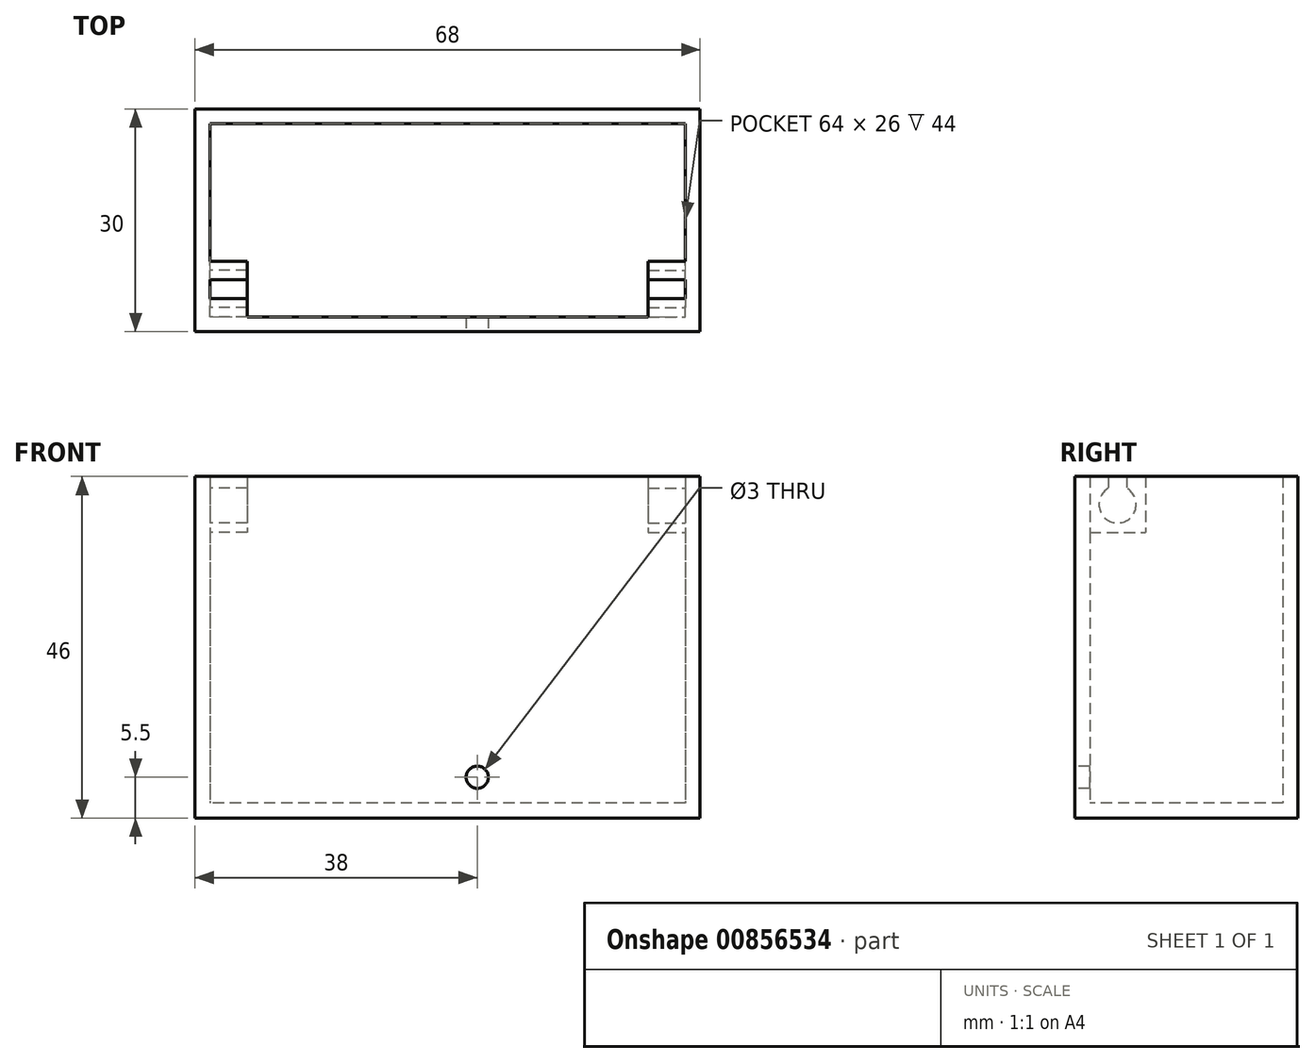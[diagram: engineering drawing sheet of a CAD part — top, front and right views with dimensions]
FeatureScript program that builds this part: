
annotation { "Feature Type Name" : "Feature", "Feature Type Description" : "" }
export const myFeature = defineFeature(function(context is Context, id is Id, definition is map)
    precondition{}
    {
        {
            var Q0;
            Q0=qCreatedBy(makeId("Top.planeOp"),FACE);
            var sketch = newSketch(context, id + "F0", { "sketchPlane" : qUnion([Q0])});
            skLineSegment(sketch, "E0.bottom", {"start": v(32, 13) * mm, "end": v(-32, 13) * mm});
            skLineSegment(sketch, "E0.top", {"start": v(32, -13) * mm, "end": v(-32, -13) * mm});
            skLineSegment(sketch, "E0.left", {"start": v(32, 13) * mm, "end": v(32, -13) * mm});
            skLineSegment(sketch, "E0.right", {"start": v(-32, 13) * mm, "end": v(-32, -13) * mm});
            skPoint(sketch, "E0.middle", {"position": v(0, 0) * mm});
            skLineSegment(sketch, "E1.bottom", {"start": v(34, 15) * mm, "end": v(-34, 15) * mm});
            skLineSegment(sketch, "E1.top", {"start": v(34, -15) * mm, "end": v(-34, -15) * mm});
            skLineSegment(sketch, "E1.left", {"start": v(34, 15) * mm, "end": v(34, -15) * mm});
            skLineSegment(sketch, "E1.right", {"start": v(-34, 15) * mm, "end": v(-34, -15) * mm});
            skSolve(sketch);
        }
        {
            var Q0;
            Q0 = qSketchRegion(id + "F0", true);
            extrude(context, id + "F1", {"entities" : qUnion([Q0]), "depth" : 46 * mm, "offsetDistance" : 25 * mm});
        }
        {
            var Q0;
            Q0 = qSketchRegion(id + "F0", true);
            var Q1;
            Q1=makeQuery(id+"F0.imprint","IMPRINT",FACE,{"disambiguationData":[TD([[makeQuery(id+"F0.imprint","IMPRINT",EDGE,{"derivedFrom":sQuery(id+"F0.wireOp",EDGE,"E0.bottom")}),1.0]])]});
            extrude(context, id + "F2", {"entities" : qUnion([Q0, Q1]), "operationType" : NewBodyOperationType.ADD, "depth" : 2 * mm, "offsetDistance" : 25 * mm});
        }
        {
            var Q0;
            Q0=makeQuery(id+"F1.opExtrude","SWEPT_FACE",FACE,{"disambiguationData":[OSD([sQuery(id+"F0.wireOp",EDGE,"E1.top")])]});
            var sketch = newSketch(context, id + "F3", { "sketchPlane" : qUnion([Q0])});
            skLineSegment(sketch, "E2", {"start": v(-34, 7) * mm, "end": v(34, 7) * mm, "construction": true});
            skCircle(sketch, "E3", {"center": v(4, 5.5) * mm, "radius": 1.5 * mm});
            skSolve(sketch);
        }
        {
            var Q0;
            Q0=makeQuery(id+"F3.imprint","IMPRINT",FACE,{"disambiguationData":[TD([[makeQuery(id+"F3.imprint","IMPRINT",EDGE,{"derivedFrom":sQuery(id+"F3.wireOp",EDGE,"E3")}),1.0]])]});
            var Q1;
            Q1=sQuery(id+"F3.wireOp",EDGE,"E3");
            extrude(context, id + "F4", {"entities" : qUnion([Q0]), "operationType" : NewBodyOperationType.REMOVE, "surfaceEntities" : qUnion([Q1]), "oppositeDirection" : true, "depth" : 3 * mm, "offsetDistance" : 25 * mm});
        }
        {
            var Q0;
            Q0=makeQuery(id+"F1.opExtrude","SWEPT_FACE",FACE,{"disambiguationData":[OSD([sQuery(id+"F0.wireOp",EDGE,"E0.right")])]});
            var sketch = newSketch(context, id + "F5", { "sketchPlane" : qUnion([Q0])});
            skLineSegment(sketch, "E4.bottom", {"start": v(-13, 46) * mm, "end": v(-5.5, 46) * mm});
            skLineSegment(sketch, "E4.top", {"start": v(-13, 38.5) * mm, "end": v(-5.5, 38.5) * mm});
            skLineSegment(sketch, "E4.left", {"start": v(-13, 46) * mm, "end": v(-13, 38.5) * mm});
            skLineSegment(sketch, "E4.right", {"start": v(-5.5, 46) * mm, "end": v(-5.5, 38.5) * mm});
            skLineSegment(sketch, "E5.bottom", {"start": v(-8, 46) * mm, "end": v(-10.5, 46) * mm});
            skLineSegment(sketch, "E5.top", {"start": v(-8, 38.5) * mm, "end": v(-10.5, 38.5) * mm});
            skLineSegment(sketch, "E5.left", {"start": v(-8, 46) * mm, "end": v(-8, 44.42) * mm});
            skLineSegment(sketch, "E5.right", {"start": v(-10.5, 46) * mm, "end": v(-10.5, 44.42) * mm});
            skPoint(sketch, "E5.middle", {"position": v(-9.25, 42.25) * mm});
            skPoint(sketch, "E6.orphan", {"position": v(-9.25, 38.5) * mm});
            skPoint(sketch, "E7.start.orphan", {"position": v(-9.25, 46) * mm});
            skArc(sketch, "E8", {"start": v(-10.5, 44.42) * mm, "mid": v(-9.25, 39.75) * mm, "end": v(-8, 44.42) * mm});
            skSolve(sketch);
        }
        {
            var Q0;
            {var subQ3=sQuery(id+"F5.wireOp",EDGE,"E4.left");Q0=makeQuery(id+"F5.imprint","IMPRINT",FACE,{"disambiguationData":[TD([[makeQuery(id+"F5.imprint","IMPRINT",EDGE,{"derivedFrom":subQ3}),1.0]])]});}
            extrude(context, id + "F6", {"entities" : qUnion([Q0]), "operationType" : NewBodyOperationType.ADD, "depth" : 5 * mm, "offsetDistance" : 25 * mm});
        }
        {
            var Q0;
            Q0=makeQuery(id+"F1.opExtrude","SWEPT_FACE",FACE,{"disambiguationData":[OSD([sQuery(id+"F0.wireOp",EDGE,"E0.left")])]});
            var sketch = newSketch(context, id + "F7", { "sketchPlane" : qUnion([Q0])});
            skLineSegment(sketch, "E9.bottom", {"start": v(13, 46) * mm, "end": v(5.5, 46) * mm});
            skLineSegment(sketch, "E9.top", {"start": v(13, 38.5) * mm, "end": v(5.5, 38.5) * mm});
            skLineSegment(sketch, "E9.left", {"start": v(13, 46) * mm, "end": v(13, 38.5) * mm});
            skLineSegment(sketch, "E9.right", {"start": v(5.5, 46) * mm, "end": v(5.5, 38.5) * mm});
            skArc(sketch, "E10", {"start": v(8, 44.42) * mm, "mid": v(9.25, 39.75) * mm, "end": v(10.5, 44.42) * mm});
            skLineSegment(sketch, "E11.bottom", {"start": v(10.5, 46) * mm, "end": v(8, 46) * mm});
            skLineSegment(sketch, "E11.top", {"start": v(10.5, 38.5) * mm, "end": v(8, 38.5) * mm});
            skLineSegment(sketch, "E11.left", {"start": v(10.5, 46) * mm, "end": v(10.5, 44.42) * mm});
            skLineSegment(sketch, "E11.right", {"start": v(8, 46) * mm, "end": v(8, 44.42) * mm});
            skPoint(sketch, "E12.trimOffspring.end.orphan", {"position": v(9.25, 38.5) * mm});
            skPoint(sketch, "E13.start.orphan", {"position": v(9.25, 46) * mm});
            skSolve(sketch);
        }
        {
            var Q0;
            {var subQ3=sQuery(id+"F7.wireOp",EDGE,"E9.left");Q0=makeQuery(id+"F7.imprint","IMPRINT",FACE,{"disambiguationData":[TD([[makeQuery(id+"F7.imprint","IMPRINT",EDGE,{"derivedFrom":subQ3}),-1.0]])]});}
            extrude(context, id + "F8", {"entities" : qUnion([Q0]), "operationType" : NewBodyOperationType.ADD, "depth" : 5 * mm, "offsetDistance" : 25 * mm});
        }
    });
